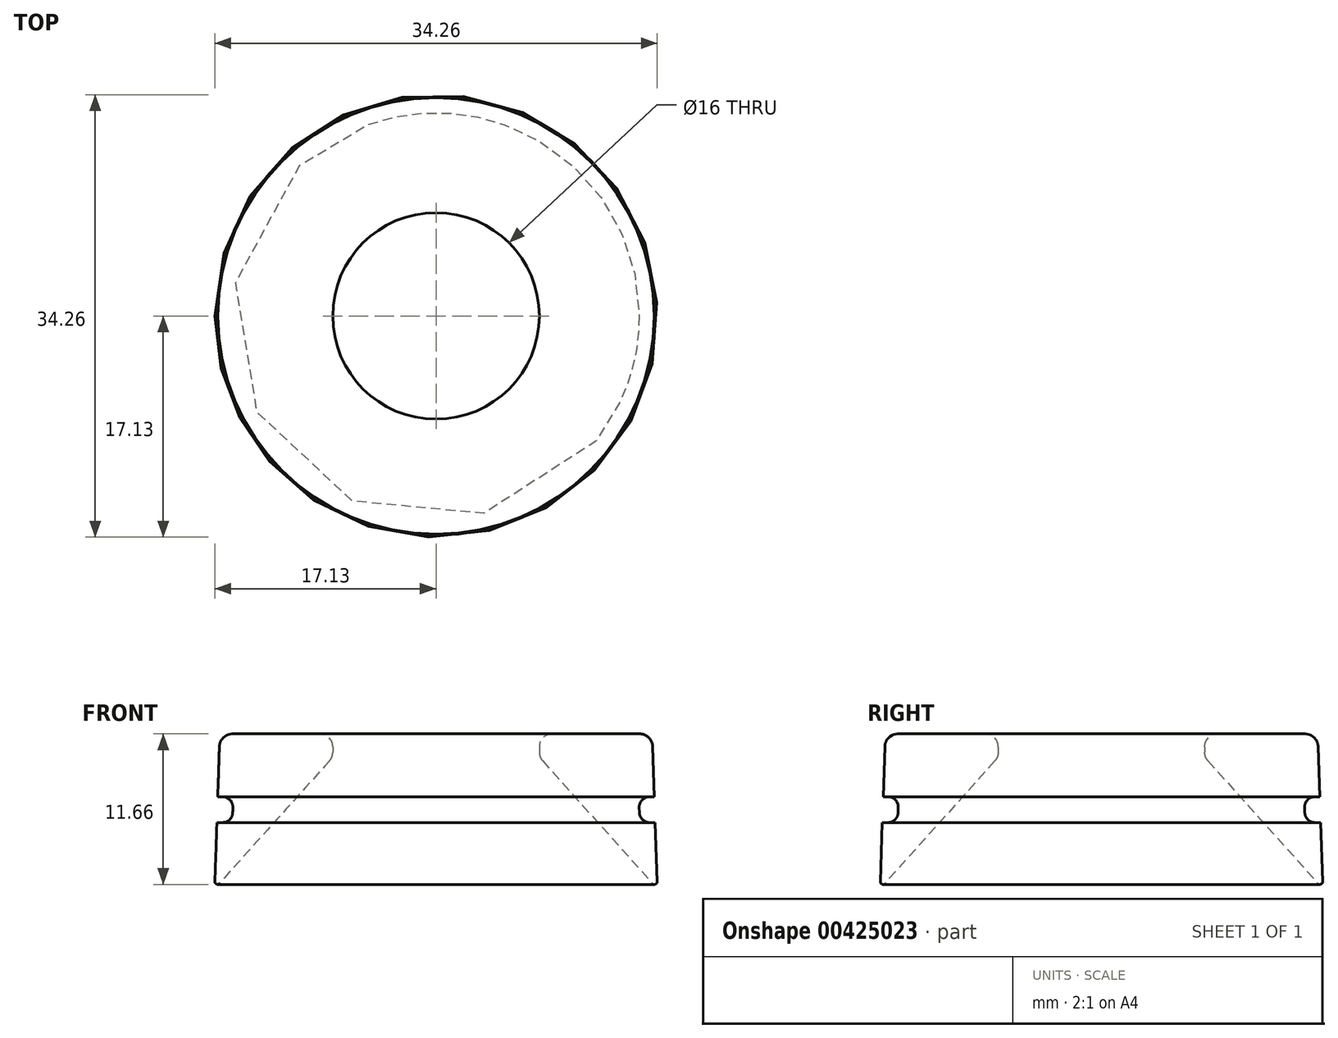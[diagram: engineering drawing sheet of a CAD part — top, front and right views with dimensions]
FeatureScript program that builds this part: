
annotation { "Feature Type Name" : "Feature", "Feature Type Description" : "" }
export const myFeature = defineFeature(function(context is Context, id is Id, definition is map)
    precondition{}
    {
        {
            var Q0;
            Q0=qCreatedBy(makeId("Front.planeOp"),FACE);
            var sketch = newSketch(context, id + "F0", { "sketchPlane" : qUnion([Q0])});
            skLineSegment(sketch, "E0", {"start": v(17.15, 0) * mm, "end": v(16.75, 12) * mm});
            skLineSegment(sketch, "E1", {"start": v(17.15, 0) * mm, "end": v(6.38, 12) * mm});
            skLineSegment(sketch, "E2", {"start": v(0, 0) * mm, "end": v(0, 9.48) * mm, "construction": true});
            skLineSegment(sketch, "E3.bottom", {"start": v(16.91, 7.13) * mm, "end": v(15.71, 7.13) * mm});
            skLineSegment(sketch, "E3.top", {"start": v(16.98, 5.13) * mm, "end": v(15.78, 5.13) * mm});
            skLineSegment(sketch, "E3.left", {"start": v(16.91, 7.13) * mm, "end": v(16.98, 5.13) * mm});
            skLineSegment(sketch, "E3.right", {"start": v(15.71, 7.13) * mm, "end": v(15.78, 5.13) * mm});
            skLineSegment(sketch, "E4", {"start": v(16.75, 12) * mm, "end": v(6.38, 12) * mm});
            skLineSegment(sketch, "E5", {"start": v(8, 12) * mm, "end": v(8, 10.2) * mm});
            skSolve(sketch);
        }
        {
            var Q0;
            {var subQ7=sQuery(id+"F0.wireOp",EDGE,"E3.bottom");Q0=makeQuery(id+"F0.imprint","IMPRINT",FACE,{"disambiguationData":[TD([[makeQuery(id+"F0.imprint","IMPRINT",EDGE,{"derivedFrom":subQ7}),-1.0]])]});}
            var Q1;
            Q1=sQuery(id+"F0.wireOp",EDGE,"E2");
            revolve(context, id + "F1", {"entities" : qUnion([Q0]), "axis" : qUnion([Q1]), "revolveType" : RevolveType.FULL});
        }
        {
            var Q0;
            Q0=makeQuery(id+"F1.opRevolve","SWEPT_EDGE",EDGE,{"disambiguationData":[OSD([sQuery(id+"F0.wireOp",EDGE,"E0"),sQuery(id+"F0.wireOp",EDGE,"E4")])]});
            var Q1;
            Q1=makeQuery(id+"F1.opRevolve","SWEPT_FACE",FACE,{"disambiguationData":[OSD([sQuery(id+"F0.wireOp",EDGE,"E5")])]});
            fillet(context, id + "F2", {"entities" : qUnion([Q0, Q1]), "radius" : 1 * mm, "tangentPropagation" : true, "allowEdgeOverflow" : false});
        }
        {
            var Q0;
            Q0=makeQuery(id+"F1.opRevolve","SWEPT_EDGE",EDGE,{"disambiguationData":[OSD([sQuery(id+"F0.wireOp",EDGE,"E3.bottom"),sQuery(id+"F0.wireOp",EDGE,"E3.right")])]});
            var Q1;
            Q1=makeQuery(id+"F1.opRevolve","SWEPT_EDGE",EDGE,{"disambiguationData":[OSD([sQuery(id+"F0.wireOp",EDGE,"E3.top"),sQuery(id+"F0.wireOp",EDGE,"E3.right")])]});
            fillet(context, id + "F3", {"entities" : qUnion([Q0, Q1]), "radius" : .8 * mm, "tangentPropagation" : true, "allowEdgeOverflow" : false});
        }
        {
            var Q0;
            Q0=makeQuery(id+"F1.opRevolve","SWEPT_EDGE",EDGE,{"disambiguationData":[OSD([sQuery(id+"F0.wireOp",EDGE,"E0"),sQuery(id+"F0.wireOp",EDGE,"E1")])]});
            fillet(context, id + "F4", {"entities" : qUnion([Q0]), "radius" : .2 * mm, "tangentPropagation" : true, "allowEdgeOverflow" : false});
        }
    });
